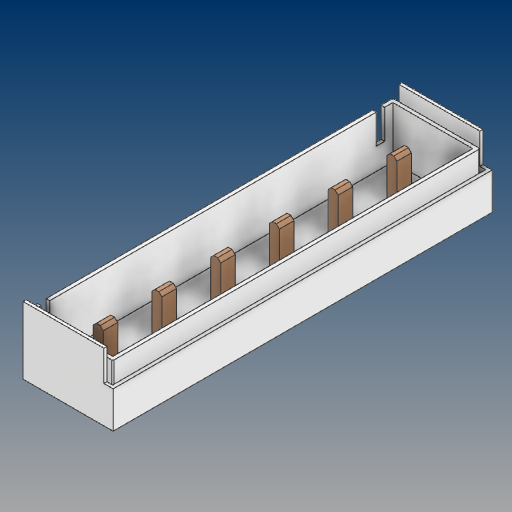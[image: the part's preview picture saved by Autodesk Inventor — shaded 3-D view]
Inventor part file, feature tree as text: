
AUTODESK INVENTOR PART (.ipt)
format: ipt  version: 2021 (Build 250183000, 183)  size: 173,568 bytes
history: native  units: mm
features: chamfer x1, other x1
ambient origin geometry x8: Origin, YZ Plane, XZ Plane, XY Plane, X Axis, Y Axis, Z Axis, Center Point
bodies: Solid1 (feature_tree), Solid2 (feature_tree)
feature tree (2):
  chamfer  "Chamfer2"  [1 undecoded]
  other  "Boss-Extrude4"
note: 1 required parameter value undecoded (feature->parameter linkage not recoverable at this tier; creation-order binding heuristic only, values carry confidence <= 0.55)
